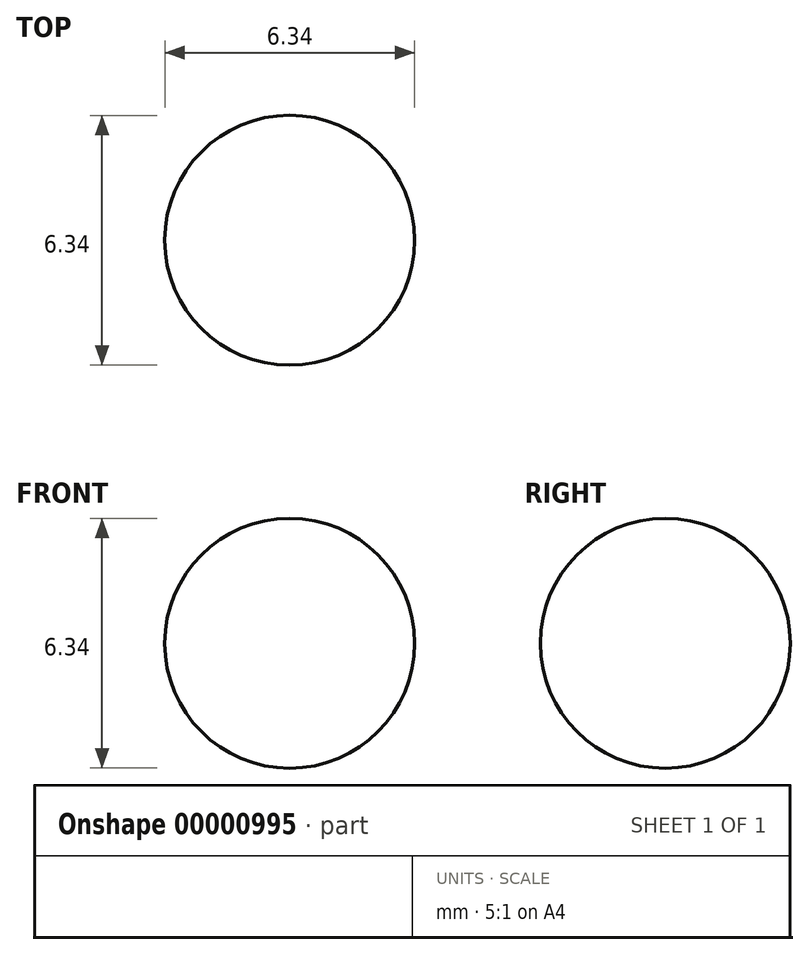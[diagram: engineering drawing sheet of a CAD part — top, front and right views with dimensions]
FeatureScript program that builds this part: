
annotation { "Feature Type Name" : "Feature", "Feature Type Description" : "" }
export const myFeature = defineFeature(function(context is Context, id is Id, definition is map)
    precondition{}
    {
        {
            var Q0;
            Q0=qCreatedBy(makeId("Front.planeOp"),FACE);
            var sketch = newSketch(context, id + "F0", { "sketchPlane" : qUnion([Q0])});
            skArc(sketch, "E0", {"start": v(0, -3.17) * mm, "mid": v(3.17, 0) * mm, "end": v(0, 3.17) * mm});
            skLineSegment(sketch, "E1", {"start": v(0, -4.74) * mm, "end": v(0, 4.52) * mm, "construction": true});
            skLineSegment(sketch, "E2", {"start": v(0, 3.17) * mm, "end": v(0, -3.17) * mm});
            skSolve(sketch);
        }
        {
            var Q0;
            Q0=makeQuery(id+"F0.imprint","IMPRINT",FACE,{"disambiguationData":[TD([[makeQuery(id+"F0.imprint","IMPRINT",EDGE,{"derivedFrom":sQuery(id+"F0.wireOp",EDGE,"E0")}),1.0]])]});
            var Q1;
            Q1=sQuery(id+"F0.wireOp",EDGE,"E1");
            revolve(context, id + "F1", {"entities" : qUnion([Q0]), "axis" : qUnion([Q1]), "revolveType" : RevolveType.FULL});
        }
    });
